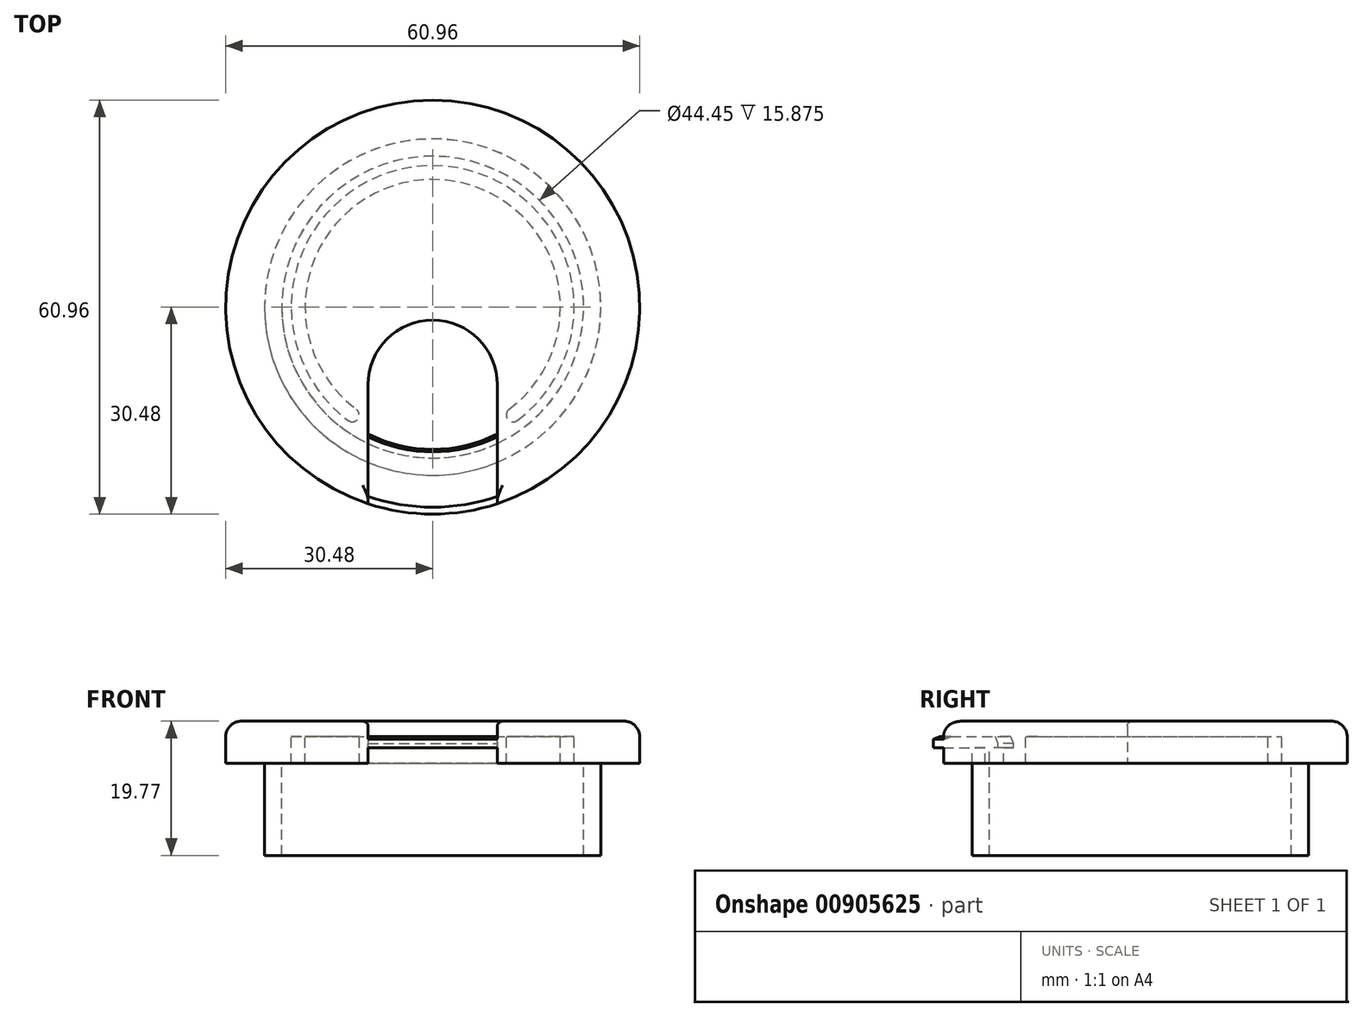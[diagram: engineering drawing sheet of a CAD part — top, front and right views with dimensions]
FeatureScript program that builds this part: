
annotation { "Feature Type Name" : "Feature", "Feature Type Description" : "" }
export const myFeature = defineFeature(function(context is Context, id is Id, definition is map)
    precondition{}
    {
        {
            var Q0;
            Q0=qCreatedBy(makeId("Top.planeOp"),FACE);
            var sketch = newSketch(context, id + "F0", { "sketchPlane" : qUnion([Q0])});
            skCircle(sketch, "E0", {"center": v(0, 0) * mm, "radius": 20.96 * mm});
            skCircle(sketch, "E1", {"center": v(0, 0) * mm, "radius": 30.48 * mm});
            skSolve(sketch);
        }
        {
            var Q0;
            Q0=makeQuery(id+"F0.imprint","IMPRINT",FACE,{"disambiguationData":[TD([[makeQuery(id+"F0.imprint","IMPRINT",EDGE,{"derivedFrom":sQuery(id+"F0.wireOp",EDGE,"E0")}),-1.0]])]});
            extrude(context, id + "F1", {"entities" : qUnion([Q0]), "oppositeDirection" : true, "depth" : 1.6 * mm, "offsetDistance" : 25.4 * mm});
        }
        {
            var Q0;
            Q0=makeQuery(id+"F1.opExtrude","CAP_FACE",FACE,{"disambiguationData":[OSD([sQuery(id+"F0.wireOp",EDGE,"E0"),sQuery(id+"F0.wireOp",EDGE,"E1")])],"isStart":false});
            var sketch = newSketch(context, id + "F2", { "sketchPlane" : qUnion([Q0])});
            skCircle(sketch, "E2", {"center": v(0, 0) * mm, "radius": 22.23 * mm});
            skCircle(sketch, "E3.0", {"center": v(0, 0) * mm, "radius": 24.77 * mm});
            skSolve(sketch);
        }
        {
            var Q0;
            Q0=makeQuery(id+"F2.imprint","IMPRINT",FACE,{"disambiguationData":[TD([[makeQuery(id+"F2.imprint","IMPRINT",EDGE,{"derivedFrom":sQuery(id+"F2.wireOp",EDGE,"E2")}),-1.0]])]});
            extrude(context, id + "F3", {"entities" : qUnion([Q0]), "operationType" : NewBodyOperationType.ADD, "depth" : 15.88 * mm, "offsetDistance" : 25.4 * mm});
        }
        {
            var Q0;
            Q0=makeQuery(id+"F1.opExtrude","CAP_FACE",FACE,{"disambiguationData":[OSD([sQuery(id+"F0.wireOp",EDGE,"E0"),sQuery(id+"F0.wireOp",EDGE,"E1")])],"isStart":true});
            var sketch = newSketch(context, id + "F4", { "sketchPlane" : qUnion([Q0])});
            skCircle(sketch, "E4", {"center": v(0, 0) * mm, "radius": 30.48 * mm});
            skLineSegment(sketch, "E5", {"start": v(0, 0) * mm, "end": v(0, -30.48) * mm, "construction": true});
            skLineSegment(sketch, "E6", {"start": v(-9.52, -11.43) * mm, "end": v(9.52, -11.43) * mm, "construction": true});
            skPoint(sketch, "E7", {"position": v(0, -11.43) * mm});
            skLineSegment(sketch, "E8", {"start": v(-9.52, -11.43) * mm, "end": v(-9.52, -28.95) * mm});
            skLineSegment(sketch, "E9", {"start": v(9.52, -11.43) * mm, "end": v(9.52, -28.95) * mm});
            skArc(sketch, "E10", {"start": v(9.52, -11.43) * mm, "mid": v(0, -1.9) * mm, "end": v(-9.52, -11.43) * mm});
            skSolve(sketch);
        }
        {
            var Q0;
            Q0=makeQuery(id+"F4.imprint","IMPRINT",FACE,{"disambiguationData":[TD([[makeQuery(id+"F4.imprint","IMPRINT",EDGE,{"derivedFrom":sQuery(id+"F4.wireOp",EDGE,"E4")}),1.0]])]});
            var Q1;
            Q1=makeQuery(id+"F4.imprint","IMPRINT",FACE,{"disambiguationData":[TD([[makeQuery(id+"F4.imprint","IMPRINT",EDGE,{"derivedFrom":makeQuery(id+"F1.opExtrude","CAP_EDGE",EDGE,{"disambiguationData":[OSD([sQuery(id+"F0.wireOp",EDGE,"E0")])],"isStart":true})}),1.0]])]});
            extrude(context, id + "F5", {"entities" : qUnion([Q0, Q1]), "depth" : 2.3 * mm, "offsetDistance" : 25.4 * mm});
        }
        {
            var Q0;
            Q0=makeQuery(id+"F5.opExtrude","CAP_FACE",FACE,{"disambiguationData":[OSD([sQuery(id+"F4.wireOp",EDGE,"E4")])],"isStart":false});
            fillet(context, id + "F6", {"entities" : qUnion([Q0]), "radius" : 2.3 * mm, "tangentPropagation" : true, "allowEdgeOverflow" : false});
        }
        {
            var Q0;
            {var subQ0=sQuery(id+"F4.wireOp",EDGE,"E10");Q0=makeQuery(id+"F4.imprint","IMPRINT",FACE,{"disambiguationData":[TD([[makeQuery(id+"F4.imprint","IMPRINT",EDGE,{"derivedFrom":subQ0}),1.0]])]});}
            var Q1;
            {var subQ0=sQuery(id+"F4.wireOp",EDGE,"E8");var subQ1=sQuery(id+"F4.wireOp",EDGE,"E4");var subQ2=makeQuery(id+"F4.imprint","INTERSECT",VERTEX,{"derivedFrom":[subQ1,subQ0]});Q1=makeQuery(id+"F4.imprint","IMPRINT",FACE,{"disambiguationData":[TD([[makeQuery(id+"F4.imprint","IMPRINT",EDGE,{"disambiguationData":[TD([[subQ2,-1.0]])],"derivedFrom":subQ1}),1.0]])]});}
            extrude(context, id + "F7", {"entities" : qUnion([Q0, Q1]), "operationType" : NewBodyOperationType.REMOVE, "endBound" : BoundingType.THROUGH_ALL, "depth" : 25.4 * mm, "offsetDistance" : 25.4 * mm});
        }
        {
            var Q0;
            Q0=makeQuery(id+"F7.boolean.opBoolean","INTERSECT",EDGE,{"derivedFrom":[makeQuery(id+"F5.opExtrude","CAP_FACE",FACE,{"disambiguationData":[OSD([sQuery(id+"F4.wireOp",EDGE,"E4")])],"isStart":false}),makeQuery(id+"F7.opExtrude","SWEPT_FACE",FACE,{"disambiguationData":[OSD([sQuery(id+"F4.wireOp",EDGE,"E8")])]})]});
            var Q1;
            Q1=makeQuery(id+"F7.boolean.opBoolean","INTERSECT",EDGE,{"derivedFrom":[makeQuery(id+"F5.opExtrude","CAP_FACE",FACE,{"disambiguationData":[OSD([sQuery(id+"F4.wireOp",EDGE,"E4")])],"isStart":false}),makeQuery(id+"F7.opExtrude","SWEPT_FACE",FACE,{"disambiguationData":[OSD([sQuery(id+"F4.wireOp",EDGE,"E10")])]})]});
            var Q2;
            Q2=makeQuery(id+"F7.boolean.opBoolean","INTERSECT",EDGE,{"derivedFrom":[makeQuery(id+"F5.opExtrude","CAP_FACE",FACE,{"disambiguationData":[OSD([sQuery(id+"F4.wireOp",EDGE,"E4")])],"isStart":false}),makeQuery(id+"F7.opExtrude","SWEPT_FACE",FACE,{"disambiguationData":[OSD([sQuery(id+"F4.wireOp",EDGE,"E9")])]})]});
            fillet(context, id + "F8", {"entities" : qUnion([Q0, Q1, Q2]), "radius" : 0.76 * mm, "allowEdgeOverflow" : false});
        }
        {
            var Q0;
            Q0=makeQuery(id+"F5.opExtrude","CAP_FACE",FACE,{"disambiguationData":[OSD([sQuery(id+"F4.wireOp",EDGE,"E4")])],"isStart":true});
            var sketch = newSketch(context, id + "F9", { "sketchPlane" : qUnion([Q0])});
            skArc(sketch, "E11", {"start": v(12.45, 16.7) * mm, "mid": v(0, -20.83) * mm, "end": v(-12.45, 16.7) * mm});
            skArc(sketch, "E12.0", {"start": v(11.24, 15.07) * mm, "mid": v(0, -18.8) * mm, "end": v(-11.24, 15.07) * mm});
            skLineSegment(sketch, "E13", {"start": v(-11.24, 15.07) * mm, "end": v(-12.45, 16.7) * mm, "construction": true});
            skLineSegment(sketch, "E14", {"start": v(11.24, 15.07) * mm, "end": v(12.45, 16.7) * mm, "construction": true});
            skLineSegment(sketch, "E15", {"start": v(-12.45, 16.7) * mm, "end": v(-11.16, 17.66) * mm, "construction": true});
            skArc(sketch, "E16", {"start": v(-11.24, 15.07) * mm, "mid": v(-11.03, 16.49) * mm, "end": v(-12.45, 16.7) * mm});
            skLineSegment(sketch, "E17", {"start": v(12.45, 16.7) * mm, "end": v(11.36, 17.51) * mm, "construction": true});
            skArc(sketch, "E18", {"start": v(12.45, 16.7) * mm, "mid": v(11.03, 16.49) * mm, "end": v(11.24, 15.07) * mm});
            skSolve(sketch);
        }
        {
            var Q0;
            Q0=makeQuery(id+"F9.imprint","IMPRINT",FACE,{"disambiguationData":[TD([[makeQuery(id+"F9.imprint","IMPRINT",EDGE,{"derivedFrom":sQuery(id+"F9.wireOp",EDGE,"E11")}),-1.0]])]});
            extrude(context, id + "F10", {"entities" : qUnion([Q0]), "operationType" : NewBodyOperationType.ADD, "depth" : 3.94 * mm, "offsetDistance" : 25.4 * mm});
        }
        {
            var Q0;
            Q0=makeQuery(id+"F1.opExtrude","CAP_EDGE",EDGE,{"disambiguationData":[OSD([sQuery(id+"F0.wireOp",EDGE,"E1")])],"isStart":true});
            chamfer(context, id + "F11", {"entities" : qUnion([Q0]), "chamferType" : ChamferType.TWO_OFFSETS, "width1" : 0.38 * mm, "oppositeDirection" : false, "width2" : 1.02 * mm, "tangentPropagation" : true});
        }
        {
            var Q0;
            Q0=makeQuery(id+"F1.opExtrude","CAP_EDGE",EDGE,{"disambiguationData":[OSD([sQuery(id+"F0.wireOp",EDGE,"E0")])],"isStart":true});
            chamfer(context, id + "F12", {"entities" : qUnion([Q0]), "chamferType" : ChamferType.TWO_OFFSETS, "width1" : 1.02 * mm, "oppositeDirection" : false, "width2" : 0.38 * mm, "tangentPropagation" : true});
        }
    });
